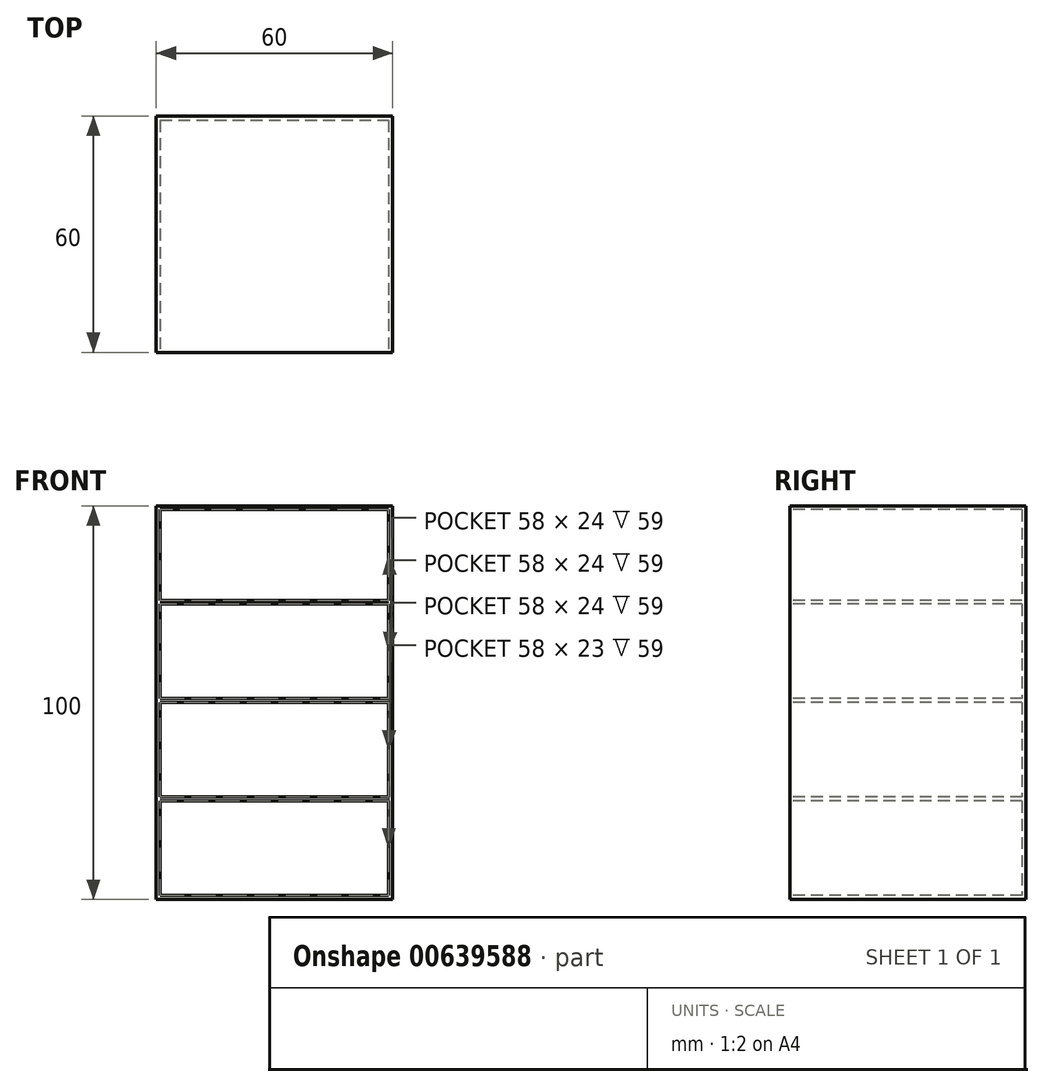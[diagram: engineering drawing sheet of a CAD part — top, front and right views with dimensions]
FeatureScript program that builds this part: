
annotation { "Feature Type Name" : "Feature", "Feature Type Description" : "" }
export const myFeature = defineFeature(function(context is Context, id is Id, definition is map)
    precondition{}
    {
        {
            var Q0;
            Q0=qCreatedBy(makeId("Top.planeOp"),FACE);
            var sketch = newSketch(context, id + "F0", { "sketchPlane" : qUnion([Q0])});
            skLineSegment(sketch, "E0.bottom", {"start": v(-30, 30) * mm, "end": v(30, 30) * mm});
            skLineSegment(sketch, "E0.top", {"start": v(-30, -30) * mm, "end": v(30, -30) * mm});
            skLineSegment(sketch, "E0.left", {"start": v(-30, 30) * mm, "end": v(-30, -30) * mm});
            skLineSegment(sketch, "E0.right", {"start": v(30, 30) * mm, "end": v(30, -30) * mm});
            skPoint(sketch, "E0.middle", {"position": v(0, 0) * mm});
            skSolve(sketch);
        }
        {
            var Q0;
            Q0=makeQuery(id+"F0.imprint","IMPRINT",FACE,{"disambiguationData":[TD([[makeQuery(id+"F0.imprint","IMPRINT",EDGE,{"derivedFrom":sQuery(id+"F0.wireOp",EDGE,"E0.bottom")}),-1.0]])]});
            extrude(context, id + "F1", {"entities" : qUnion([Q0]), "endBound" : BoundingType.SYMMETRIC, "depth" : 100 * mm, "offsetDistance" : 25 * mm});
        }
        {
            var Q0;
            Q0=makeQuery(id+"F1.opExtrude","SWEPT_FACE",FACE,{"disambiguationData":[OSD([sQuery(id+"F0.wireOp",EDGE,"E0.top")])]});
            var Q1;
            Q1=makeQuery(id+"F1.opExtrude","SWEPT_BODY",BODY,{"disambiguationData":[OSD([sQuery(id+"F0.wireOp",EDGE,"E0.bottom"),sQuery(id+"F0.wireOp",EDGE,"E0.top"),sQuery(id+"F0.wireOp",EDGE,"E0.left"),sQuery(id+"F0.wireOp",EDGE,"E0.right")])]});
            shell(context, id + "F2", {"entities" : qUnion([Q0]), "parts" : qUnion([Q1]), "thickness" : 1 * mm});
        }
        {
            var Q0;
            Q0=makeQuery(id+"F1.opExtrude","CAP_FACE",FACE,{"disambiguationData":[OSD([sQuery(id+"F0.wireOp",EDGE,"E0.bottom"),sQuery(id+"F0.wireOp",EDGE,"E0.top"),sQuery(id+"F0.wireOp",EDGE,"E0.left"),sQuery(id+"F0.wireOp",EDGE,"E0.right")])],"isStart":false});
            cPlane(context, id + "F3", {"entities" : qUnion([Q0]), "cplaneType" : CPlaneType.OFFSET, "offset" : 25 * mm, "oppositeDirection" : true, "width" : 150 * mm, "height" : 150 * mm});
        }
        {
            var Q0;
            Q0=qCreatedBy(makeId("Top.planeOp"),FACE);
            cPlane(context, id + "F4", {"entities" : qUnion([Q0]), "cplaneType" : CPlaneType.OFFSET, "offset" : 25 * mm, "oppositeDirection" : true, "width" : 150 * mm, "height" : 150 * mm});
        }
        {
            var Q0;
            Q0=qCreatedBy(id+"F3.planeOp",FACE);
            var sketch = newSketch(context, id + "F5", { "sketchPlane" : qUnion([Q0])});
            skLineSegment(sketch, "E1.bottom", {"start": v(-30, 30) * mm, "end": v(30, 30) * mm});
            skLineSegment(sketch, "E1.top", {"start": v(-30, -30) * mm, "end": v(30, -30) * mm});
            skLineSegment(sketch, "E1.left", {"start": v(-30, 30) * mm, "end": v(-30, -30) * mm});
            skLineSegment(sketch, "E1.right", {"start": v(30, 30) * mm, "end": v(30, -30) * mm});
            skPoint(sketch, "E1.middle", {"position": v(0, 0) * mm});
            skSolve(sketch);
        }
        {
            var Q0;
            Q0=makeQuery(id+"F5.imprint","IMPRINT",FACE,{"disambiguationData":[TD([[makeQuery(id+"F5.imprint","IMPRINT",EDGE,{"derivedFrom":sQuery(id+"F5.wireOp",EDGE,"E1.bottom")}),-1.0]])]});
            extrude(context, id + "F6", {"entities" : qUnion([Q0]), "operationType" : NewBodyOperationType.ADD, "depth" : 1 * mm, "offsetDistance" : 25 * mm});
        }
        {
            var Q0;
            Q0=qCreatedBy(makeId("Top.planeOp"),FACE);
            var sketch = newSketch(context, id + "F7", { "sketchPlane" : qUnion([Q0])});
            skLineSegment(sketch, "E2.bottom", {"start": v(-30, 30) * mm, "end": v(30, 30) * mm});
            skLineSegment(sketch, "E2.top", {"start": v(-30, -30) * mm, "end": v(30, -30) * mm});
            skLineSegment(sketch, "E2.left", {"start": v(-30, 30) * mm, "end": v(-30, -30) * mm});
            skLineSegment(sketch, "E2.right", {"start": v(30, 30) * mm, "end": v(30, -30) * mm});
            skPoint(sketch, "E2.middle", {"position": v(0, 0) * mm});
            skSolve(sketch);
        }
        {
            var Q0;
            Q0 = qSketchRegion(id + "F7", true);
            extrude(context, id + "F8", {"entities" : qUnion([Q0]), "operationType" : NewBodyOperationType.ADD, "depth" : 1 * mm, "offsetDistance" : 25 * mm});
        }
        {
            var Q0;
            Q0=qCreatedBy(id+"F4.planeOp",FACE);
            var sketch = newSketch(context, id + "F9", { "sketchPlane" : qUnion([Q0])});
            skLineSegment(sketch, "E3.bottom", {"start": v(-30, 30) * mm, "end": v(30, 30) * mm});
            skLineSegment(sketch, "E3.top", {"start": v(-30, -30) * mm, "end": v(30, -30) * mm});
            skLineSegment(sketch, "E3.left", {"start": v(-30, 30) * mm, "end": v(-30, -30) * mm});
            skLineSegment(sketch, "E3.right", {"start": v(30, 30) * mm, "end": v(30, -30) * mm});
            skPoint(sketch, "E3.middle", {"position": v(0, 0) * mm});
            skSolve(sketch);
        }
        {
            var Q0;
            Q0 = qSketchRegion(id + "F9", true);
            extrude(context, id + "F10", {"entities" : qUnion([Q0]), "operationType" : NewBodyOperationType.ADD, "depth" : 1 * mm, "offsetDistance" : 25 * mm});
        }
    });
